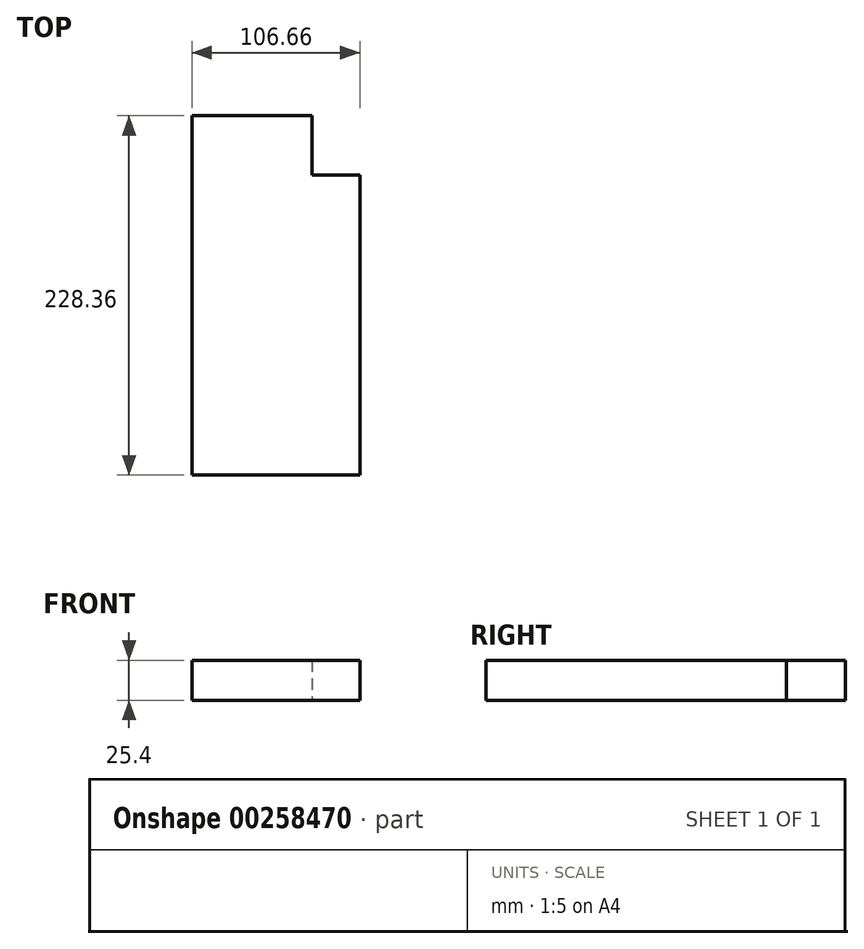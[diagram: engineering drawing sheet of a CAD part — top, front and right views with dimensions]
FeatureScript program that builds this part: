
annotation { "Feature Type Name" : "Feature", "Feature Type Description" : "" }
export const myFeature = defineFeature(function(context is Context, id is Id, definition is map)
    precondition{}
    {
        {
            var Q0;
            Q0=qCreatedBy(makeId("Top.planeOp"),FACE);
            var sketch = newSketch(context, id + "F0", { "sketchPlane" : qUnion([Q0])});
            skLineSegment(sketch, "E0.bottom", {"start": v(-53.33, 114.18) * mm, "end": v(53.33, 114.18) * mm});
            skLineSegment(sketch, "E0.top", {"start": v(-53.33, -114.18) * mm, "end": v(53.33, -114.18) * mm});
            skLineSegment(sketch, "E0.left", {"start": v(-53.33, 114.18) * mm, "end": v(-53.33, -114.18) * mm});
            skLineSegment(sketch, "E0.right", {"start": v(53.33, 114.18) * mm, "end": v(53.33, -114.18) * mm});
            skPoint(sketch, "E0.middle", {"position": v(0, 0) * mm});
            skLineSegment(sketch, "E1", {"start": v(22.8, 114.18) * mm, "end": v(22.8, 76.56) * mm});
            skLineSegment(sketch, "E2", {"start": v(22.8, 76.56) * mm, "end": v(53.33, 76.56) * mm});
            skSolve(sketch);
        }
        {
            var Q0;
            {var subQ1=sQuery(id+"F0.wireOp",EDGE,"E0.top");Q0=makeQuery(id+"F0.imprint","IMPRINT",FACE,{"disambiguationData":[TD([[makeQuery(id+"F0.imprint","IMPRINT",EDGE,{"derivedFrom":subQ1}),1.0]])]});}
            extrude(context, id + "F1", {"entities" : qUnion([Q0]), "depth" : 25.4 * mm});
        }
        {
            var Q0;
            Q0=makeQuery(id+"F1.opExtrude","SWEPT_FACE",FACE,{"disambiguationData":[OSD([sQuery(id+"F0.wireOp",EDGE,"E0.left")])]});
            var sketch = newSketch(context, id + "F2", { "sketchPlane" : qUnion([Q0])});
            skLineSegment(sketch, "E3", {"start": v(114.18, 25.4) * mm, "end": v(114.18, 88.94) * mm});
            skLineSegment(sketch, "E4", {"start": v(-114.18, 25.4) * mm, "end": v(-114.18, 88.94) * mm});
            skArc(sketch, "E5", {"start": v(114.18, 88.94) * mm, "mid": v(0, 129.08) * mm, "end": v(-114.18, 88.94) * mm});
            skSolve(sketch);
        }
    });
